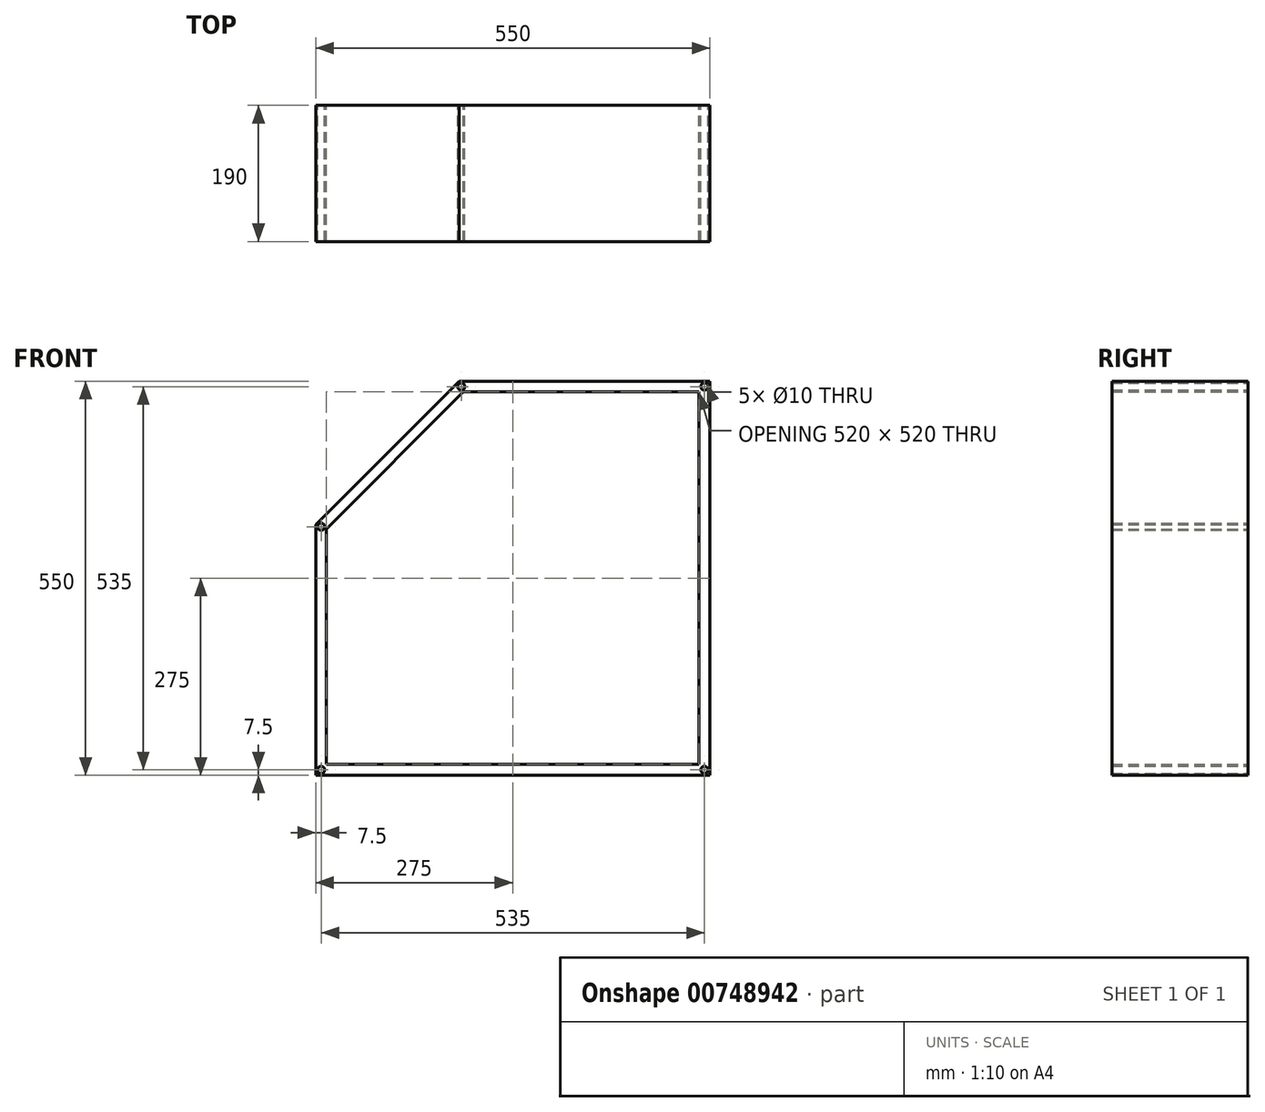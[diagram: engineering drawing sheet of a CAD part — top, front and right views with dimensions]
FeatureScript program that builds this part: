
annotation { "Feature Type Name" : "Feature", "Feature Type Description" : "" }
export const myFeature = defineFeature(function(context is Context, id is Id, definition is map)
    precondition{}
    {
        {
            var Q0;
            Q0=qCreatedBy(makeId("Front.planeOp"),FACE);
            var sketch = newSketch(context, id + "F0", { "sketchPlane" : qUnion([Q0])});
            skLineSegment(sketch, "E0.top", {"start": v(-275, -275) * mm, "end": v(275, -275) * mm});
            skLineSegment(sketch, "E0.right", {"start": v(275, 275) * mm, "end": v(275, -275) * mm});
            skPoint(sketch, "E0.middle", {"position": v(0, 0) * mm});
            skLineSegment(sketch, "E1", {"start": v(-75, 275) * mm, "end": v(275, 275) * mm});
            skLineSegment(sketch, "E2", {"start": v(-275, -275) * mm, "end": v(-275, 75) * mm});
            skLineSegment(sketch, "E3", {"start": v(275, 275) * mm, "end": v(-75, 275) * mm});
            skLineSegment(sketch, "E4", {"start": v(-75, 275) * mm, "end": v(-275, 75) * mm});
            skPoint(sketch, "E5.orphan", {"position": v(-275, 275) * mm});
            skLineSegment(sketch, "E6.0", {"start": v(-260, -260) * mm, "end": v(-260, 68.79) * mm});
            skLineSegment(sketch, "E6.1", {"start": v(-68.79, 260) * mm, "end": v(-260, 68.79) * mm});
            skLineSegment(sketch, "E6.2", {"start": v(-260, -260) * mm, "end": v(260, -260) * mm});
            skLineSegment(sketch, "E6.3", {"start": v(260, 260) * mm, "end": v(260, -260) * mm});
            skLineSegment(sketch, "E6.4", {"start": v(260, 260) * mm, "end": v(-68.79, 260) * mm});
            skLineSegment(sketch, "E7", {"start": v(260, 260) * mm, "end": v(260, -35) * mm});
            skLineSegment(sketch, "E8", {"start": v(-275, 275) * mm, "end": v(-175, 175) * mm, "construction": true});
            skCircle(sketch, "E9", {"center": v(-267.5, 71.9) * mm, "radius": 5 * mm});
            skCircle(sketch, "E10", {"center": v(-267.5, -267.5) * mm, "radius": 5 * mm});
            skCircle(sketch, "E11", {"center": v(267.5, -267.5) * mm, "radius": 5 * mm});
            skCircle(sketch, "E12.MirrorC", {"center": v(-71.9, 267.5) * mm, "radius": 5 * mm});
            skCircle(sketch, "E13.MirrorC", {"center": v(267.5, 267.5) * mm, "radius": 5 * mm});
            skLineSegment(sketch, "E14.trimOffspring", {"start": v(275, -275) * mm, "end": v(391.98, -391.98) * mm, "construction": true});
            skLineSegment(sketch, "E15", {"start": v(47.8, -47.8) * mm, "end": v(-164.4, -260) * mm, "construction": true});
            skLineSegment(sketch, "E16", {"start": v(47.8, -47.8) * mm, "end": v(260, 164.4) * mm, "construction": true});
            skLineSegment(sketch, "E17", {"start": v(260, -260) * mm, "end": v(47.8, -47.8) * mm, "construction": true});
            skLineSegment(sketch, "E18", {"start": v(-164.4, 164.4) * mm, "end": v(47.8, -47.8) * mm, "construction": true});
            skCircle(sketch, "E19", {"center": v(153.9, -153.9) * mm, "radius": 65 * mm, "construction": true});
            skCircle(sketch, "E20", {"center": v(-58.3, 58.3) * mm, "radius": 65 * mm, "construction": true});
            skLineSegment(sketch, "E21", {"start": v(260, 130) * mm, "end": v(-35, 130) * mm});
            skLineSegment(sketch, "E22", {"start": v(-35, 130) * mm, "end": v(-35, 260) * mm});
            skSolve(sketch);
        }
        {
            var Q0;
            Q0=qSketchRegion(id+"F0",true);
            extrude(context, id + "F1", {"entities" : qUnion([Q0]), "depth" : 190 * mm, "offsetDistance" : 25 * mm, "symmetric" : true});
        }
    });
